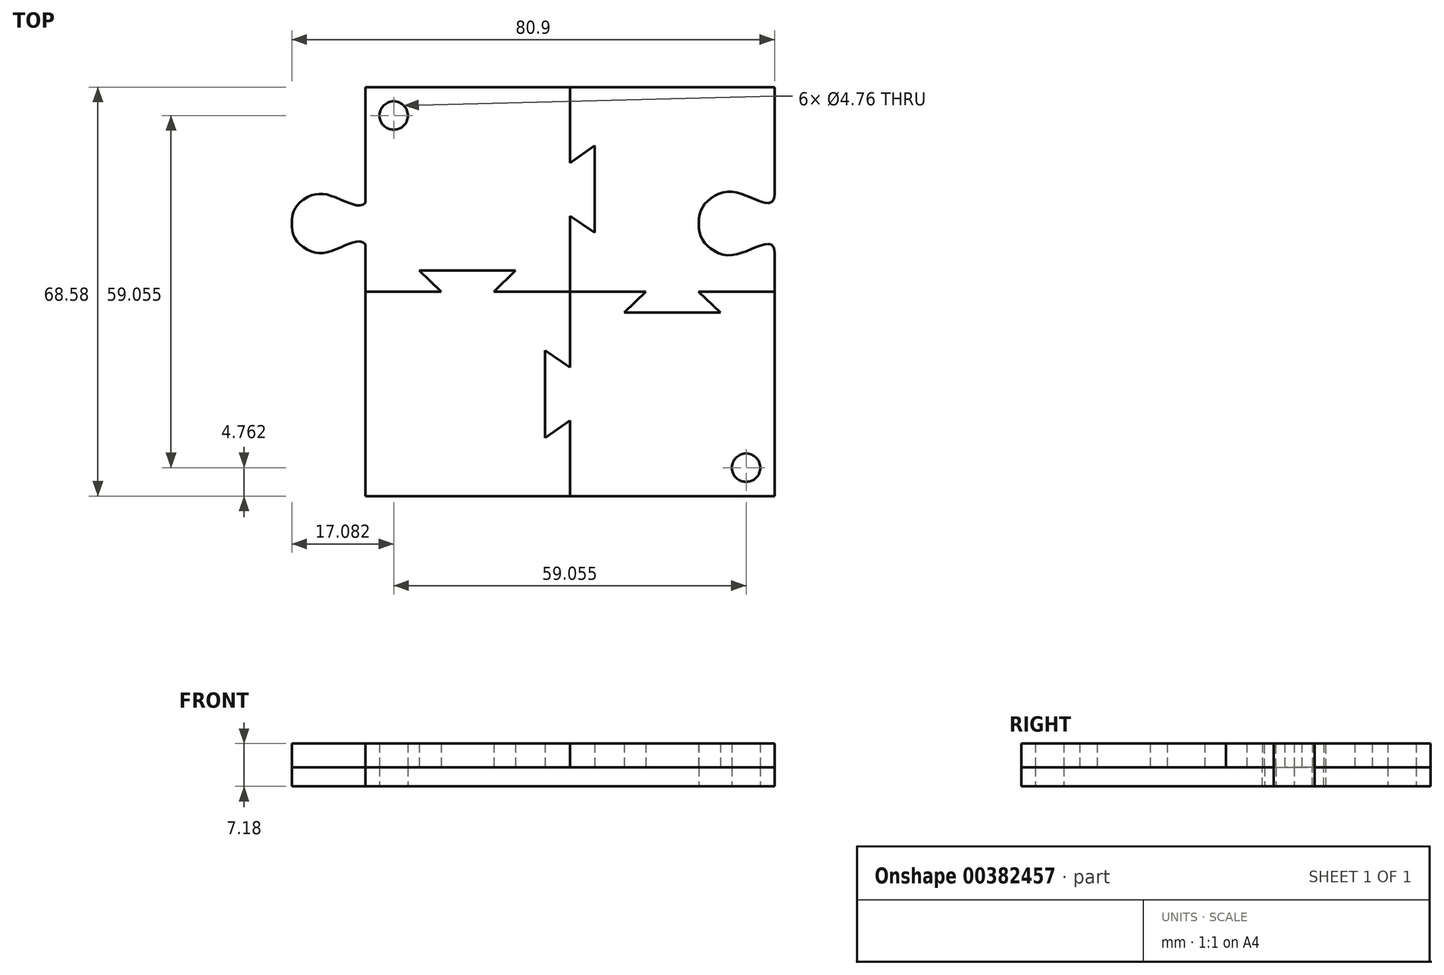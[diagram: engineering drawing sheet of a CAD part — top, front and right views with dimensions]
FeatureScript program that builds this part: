
annotation { "Feature Type Name" : "Feature", "Feature Type Description" : "" }
export const myFeature = defineFeature(function(context is Context, id is Id, definition is map)
    precondition{}
    {
        {
            var Q0;
            Q0=qCreatedBy(makeId("Top.planeOp"),FACE);
            var sketch = newSketch(context, id + "F0", { "sketchPlane" : qUnion([Q0])});
            skLineSegment(sketch, "E0.bottom", {"start": v(34.3, 34.3) * mm, "end": v(-34.3, 34.3) * mm});
            skLineSegment(sketch, "E0.top", {"start": v(34.3, -34.3) * mm, "end": v(-34.3, -34.3) * mm});
            skLineSegment(sketch, "E0.left", {"start": v(34.3, 34.3) * mm, "end": v(34.3, -34.3) * mm});
            skLineSegment(sketch, "E0.right", {"start": v(-34.3, 34.3) * mm, "end": v(-34.3, -34.3) * mm});
            skPoint(sketch, "E0.middle", {"position": v(0, 0) * mm});
            skCircle(sketch, "E1", {"center": v(-29.53, 29.53) * mm, "radius": 2.38 * mm});
            skCircle(sketch, "E2.MirrorC", {"center": v(29.53, -29.53) * mm, "radius": 2.38 * mm});
            skSolve(sketch);
        }
        {
            var Q0;
            Q0=qSketchRegion(id+"F0",true);
            extrude(context, id + "F1", {"entities" : qUnion([Q0]), "depth" : 3.17 * mm});
        }
        {
            var Q0;
            Q0=qCreatedBy(makeId("Top.planeOp"),FACE);
            var sketch = newSketch(context, id + "F2", { "sketchPlane" : qUnion([Q0])});
            skPoint(sketch, "E3", {"position": v(-34.3, 16.33) * mm});
            skPoint(sketch, "E4", {"position": v(-36.2, 14.99) * mm});
            skPoint(sketch, "E5", {"position": v(-41.66, 16.76) * mm});
            skPoint(sketch, "E6", {"position": v(-45.72, 14.99) * mm});
            skPoint(sketch, "E7", {"position": v(-47, 11.43) * mm});
            skFitSpline(sketch, "E8", {"points": [v(-34.3, 16.33) * mm, v(-36.2, 14.99) * mm, v(-41.66, 16.76) * mm, v(-45.72, 14.99) * mm, v(-47, 11.43) * mm], "startDerivative": vector(0, -24.54) * mm, "endDerivative": vector(0, -20.15) * mm});
            skLineSegment(sketch, "E9", {"start": v(-47, 11.43) * mm, "end": v(-29.95, 11.43) * mm, "construction": true});
            skFitSpline(sketch, "E10.MirrorCS", {"points": [v(-34.3, 6.53) * mm, v(-36.2, 7.87) * mm, v(-41.66, 6.1) * mm, v(-45.72, 7.87) * mm, v(-47, 11.43) * mm], "startDerivative": vector(0, 24.54) * mm, "endDerivative": vector(0, 20.15) * mm});
            skLineSegment(sketch, "E11", {"start": v(-34.3, 16.33) * mm, "end": v(-34.3, 6.53) * mm, "construction": true});
            skFitSpline(sketch, "E12.MirrorCS", {"points": [v(-34.3, 16.33) * mm, v(-32.39, 14.99) * mm, v(-26.92, 16.76) * mm, v(-22.86, 14.99) * mm, v(-21.59, 11.43) * mm], "startDerivative": vector(0, -24.54) * mm, "endDerivative": vector(0, -20.15) * mm});
            skFitSpline(sketch, "E13.MirrorCS", {"points": [v(-34.3, 6.53) * mm, v(-32.39, 7.87) * mm, v(-26.92, 6.1) * mm, v(-22.86, 7.87) * mm, v(-21.59, 11.43) * mm], "startDerivative": vector(0, 24.54) * mm, "endDerivative": vector(0, 20.15) * mm});
            skFitSpline(sketch, "E14.0", {"points": [v(-33.9, 6.53) * mm, v(-33.9, 6.8) * mm, v(-33.96, 7.3) * mm, v(-34.16, 7.77) * mm, v(-34.42, 8.07) * mm, v(-34.73, 8.28) * mm, v(-35.16, 8.4) * mm, v(-35.7, 8.38) * mm, v(-36.22, 8.27) * mm, v(-36.76, 8.1) * mm, v(-37.5, 7.83) * mm, v(-38.44, 7.42) * mm, v(-39.6, 6.94) * mm, v(-40.54, 6.64) * mm, v(-41.28, 6.5) * mm, v(-41.8, 6.46) * mm, v(-42.32, 6.5) * mm, v(-43, 6.62) * mm, v(-43.8, 6.91) * mm, v(-44.68, 7.44) * mm, v(-45.29, 7.96) * mm, v(-45.69, 8.4) * mm, v(-46.02, 8.85) * mm, v(-46.33, 9.45) * mm, v(-46.56, 10.3) * mm, v(-46.6, 11.03) * mm, v(-46.6, 11.43) * mm]});
            skFitSpline(sketch, "E14.1", {"points": [v(-33.9, 16.33) * mm, v(-33.9, 16.05) * mm, v(-33.96, 15.56) * mm, v(-34.16, 15.09) * mm, v(-34.42, 14.8) * mm, v(-34.73, 14.58) * mm, v(-35.16, 14.46) * mm, v(-35.7, 14.48) * mm, v(-36.22, 14.6) * mm, v(-36.76, 14.76) * mm, v(-37.5, 15.03) * mm, v(-38.44, 15.44) * mm, v(-39.6, 15.92) * mm, v(-40.54, 16.22) * mm, v(-41.28, 16.36) * mm, v(-41.8, 16.4) * mm, v(-42.32, 16.37) * mm, v(-43, 16.24) * mm, v(-43.8, 15.95) * mm, v(-44.68, 15.42) * mm, v(-45.29, 14.9) * mm, v(-45.69, 14.46) * mm, v(-46.02, 14.01) * mm, v(-46.33, 13.41) * mm, v(-46.56, 12.55) * mm, v(-46.6, 11.83) * mm, v(-46.6, 11.43) * mm]});
            skLineSegment(sketch, "E15", {"start": v(-34.3, 16.33) * mm, "end": v(-34.3, 6.53) * mm});
            skLineSegment(sketch, "E16", {"start": v(-34.3, 7.92) * mm, "end": v(-34.3, 14.94) * mm});
            skFitSpline(sketch, "E17.MirrorCS", {"points": [v(34.3, 16.33) * mm, v(32.39, 14.99) * mm, v(26.92, 16.76) * mm, v(22.86, 14.99) * mm, v(21.59, 11.43) * mm], "startDerivative": vector(0, -24.54) * mm, "endDerivative": vector(0, -20.15) * mm});
            skFitSpline(sketch, "E18.MirrorCS", {"points": [v(34.3, 6.53) * mm, v(32.39, 7.87) * mm, v(26.92, 6.1) * mm, v(22.86, 7.87) * mm, v(21.59, 11.43) * mm], "startDerivative": vector(0, 24.54) * mm, "endDerivative": vector(0, 20.15) * mm});
            skLineSegment(sketch, "E19", {"start": v(34.3, 16.33) * mm, "end": v(39.12, 16.33) * mm});
            skLineSegment(sketch, "E20", {"start": v(39.12, 16.33) * mm, "end": v(39.12, 6.53) * mm});
            skLineSegment(sketch, "E21", {"start": v(39.12, 6.53) * mm, "end": v(34.3, 6.53) * mm});
            skSolve(sketch);
        }
        {
            var Q0;
            Q0=makeQuery(id+"F2.imprint","IMPRINT",FACE,{"disambiguationData":[TD([[makeQuery(id+"F2.imprint","IMPRINT",EDGE,{"derivedFrom":sQuery(id+"F2.wireOp",EDGE,"E14.0")}),-1.0]])]});
            var Q1;
            Q1=makeQuery(id+"F1.opExtrude","CAP_FACE",FACE,{"disambiguationData":[OSD([sQuery(id+"F0.wireOp",EDGE,"E0.bottom"),sQuery(id+"F0.wireOp",EDGE,"E0.top"),sQuery(id+"F0.wireOp",EDGE,"E0.left"),sQuery(id+"F0.wireOp",EDGE,"E0.right"),sQuery(id+"F0.wireOp",EDGE,"E1"),sQuery(id+"F0.wireOp",EDGE,"e1648c08-8adf-473f-9b64-c467cf328ef90.MirrorC"),sQuery(id+"F0.wireOp",EDGE,"1cdcda55-2210-49d8-b5f0-9198a802923b0.MirrorC"),sQuery(id+"F0.wireOp",EDGE,"E2.MirrorC")])],"isStart":false});
            extrude(context, id + "F3", {"entities" : qUnion([Q0]), "operationType" : NewBodyOperationType.ADD, "endBound" : BoundingType.UP_TO_SURFACE, "endBoundEntityFace" : qUnion([Q1]), "depth" : 25.4 * mm});
        }
        {
            var Q0;
            Q0=qCreatedBy(makeId("Right.planeOp"),FACE);
            var sketch = newSketch(context, id + "F4", { "sketchPlane" : qUnion([Q0])});
            skLineSegment(sketch, "E22", {"start": v(0, -65.87) * mm, "end": v(0, 47.63) * mm});
            skSolve(sketch);
        }
        {
            var Q0;
            Q0=makeQuery(id+"F2.imprint","IMPRINT",FACE,{"disambiguationData":[TD([[makeQuery(id+"F2.imprint","IMPRINT",EDGE,{"derivedFrom":sQuery(id+"F2.wireOp",EDGE,"E17.MirrorCS")}),1.0]])]});
            extrude(context, id + "F5", {"entities" : qUnion([Q0]), "operationType" : NewBodyOperationType.REMOVE, "endBound" : BoundingType.THROUGH_ALL, "depth" : 25.4 * mm});
        }
        {
            var Q0;
            {var subQ0=sQuery(id+"F0.wireOp",EDGE,"E2.MirrorC");var subQ1=sQuery(id+"F0.wireOp",EDGE,"E1");var subQ2=sQuery(id+"F0.wireOp",EDGE,"E0.right");var subQ3=sQuery(id+"F0.wireOp",EDGE,"E0.left");var subQ4=sQuery(id+"F0.wireOp",EDGE,"E0.top");var subQ5=sQuery(id+"F0.wireOp",EDGE,"E0.bottom");Q0=makeQuery(id+"FDfX84p6046V9zH_1.3.F3.boolean.opBoolean","MERGE",FACE,{"derivedFrom":[makeQuery(id+"FDfX84p6046V9zH_1.2.F3.boolean.opBoolean","MERGE",FACE,{"derivedFrom":[makeQuery(id+"FDfX84p6046V9zH_1.1.F3.boolean.opBoolean","MERGE",FACE,{"derivedFrom":[makeQuery(id+"F3.boolean.opBoolean","MERGE",FACE,{"derivedFrom":[makeQuery(id+"F1.opExtrude","CAP_FACE",FACE,{"disambiguationData":[OSD([subQ5,subQ4,subQ3,subQ2,subQ1,subQ0])],"isStart":false}),makeQuery(id+"F3.opExtrude","CAP_FACE",FACE,{"disambiguationData":[OSD([subQ5,subQ4,subQ3,subQ2,subQ1,subQ0])],"isStart":false})]}),makeQuery(id+"FDfX84p6046V9zH_1.1.F3.opExtrude","CAP_FACE",FACE,{"disambiguationData":[OSD([subQ5,subQ4,subQ3,subQ2,subQ1,subQ0])],"isStart":false})]}),makeQuery(id+"FDfX84p6046V9zH_1.2.F3.opExtrude","CAP_FACE",FACE,{"disambiguationData":[OSD([subQ5,subQ4,subQ3,subQ2,subQ1,subQ0])],"isStart":false})]}),makeQuery(id+"FDfX84p6046V9zH_1.3.F3.opExtrude","CAP_FACE",FACE,{"disambiguationData":[OSD([subQ5,subQ4,subQ3,subQ2,subQ1,subQ0])],"isStart":false})]});}
            var sketch = newSketch(context, id + "F6", { "sketchPlane" : qUnion([Q0])});
            skLineSegment(sketch, "E23", {"start": v(-34.3, 0) * mm, "end": v(-21.58, 0) * mm});
            skLineSegment(sketch, "E24", {"start": v(-21.58, 0) * mm, "end": v(-25.25, 3.52) * mm});
            skLineSegment(sketch, "E25", {"start": v(0, 0) * mm, "end": v(-12.73, 0) * mm});
            skLineSegment(sketch, "E26", {"start": v(-12.73, 0) * mm, "end": v(-9.11, 3.52) * mm});
            skLineSegment(sketch, "E27", {"start": v(-9.11, 3.52) * mm, "end": v(-25.25, 3.52) * mm});
            skLineSegment(sketch, "E28.MirrorCS", {"start": v(34.3, 0) * mm, "end": v(21.58, 0) * mm});
            skLineSegment(sketch, "E29.MirrorCS", {"start": v(0, 0) * mm, "end": v(12.73, 0) * mm});
            skLineSegment(sketch, "E30.MirrorCS", {"start": v(9.11, -3.52) * mm, "end": v(25.25, -3.52) * mm});
            skLineSegment(sketch, "E31.MirrorCS", {"start": v(12.73, 0) * mm, "end": v(9.11, -3.52) * mm});
            skLineSegment(sketch, "E32.MirrorCS", {"start": v(21.58, 0) * mm, "end": v(25.25, -3.52) * mm});
            skPoint(sketch, "E33.MirrorCS.start.orphan", {"position": v(-12.73, 0) * mm});
            skPoint(sketch, "E34.MirrorCS.start.orphan", {"position": v(-21.58, 0) * mm});
            skLineSegment(sketch, "E35", {"start": v(0, 34.3) * mm, "end": v(0, 21.6) * mm});
            skLineSegment(sketch, "E36", {"start": v(0, 21.6) * mm, "end": v(4.16, 24.51) * mm});
            skLineSegment(sketch, "E37", {"start": v(0, 0) * mm, "end": v(0, 12.7) * mm});
            skLineSegment(sketch, "E38", {"start": v(0, 12.7) * mm, "end": v(4.16, 9.86) * mm});
            skLineSegment(sketch, "E39", {"start": v(4.16, 9.86) * mm, "end": v(4.16, 24.51) * mm});
            skLineSegment(sketch, "E40.MirrorCS", {"start": v(0, 0) * mm, "end": v(0, -12.7) * mm});
            skLineSegment(sketch, "E41.MirrorCS", {"start": v(0, -34.3) * mm, "end": v(0, -21.6) * mm});
            skLineSegment(sketch, "E42.MirrorCS", {"start": v(0, -12.7) * mm, "end": v(-4.16, -9.86) * mm});
            skLineSegment(sketch, "E43.MirrorCS", {"start": v(-4.16, -9.86) * mm, "end": v(-4.16, -24.51) * mm});
            skLineSegment(sketch, "E44.MirrorCS", {"start": v(0, -21.6) * mm, "end": v(-4.16, -24.51) * mm});
            skPoint(sketch, "E45.MirrorCS.start.orphan", {"position": v(0, -12.7) * mm});
            skPoint(sketch, "E46.MirrorCS.start.orphan", {"position": v(0, -21.6) * mm});
            skSolve(sketch);
        }
        {
            var Q0;
            {var subQ1=sQuery(id+"F6.wireOp",EDGE,"E28.MirrorCS");Q0=makeQuery(id+"F6.imprint","IMPRINT",FACE,{"disambiguationData":[TD([[makeQuery(id+"F6.imprint","IMPRINT",EDGE,{"derivedFrom":subQ1}),1.0]])]});}
            extrude(context, id + "F7", {"entities" : qUnion([Q0]), "depth" : 4 * mm});
        }
        {
            var Q0;
            {var subQ22=sQuery(id+"F6.wireOp",EDGE,"E23");Q0=makeQuery(id+"F6.imprint","IMPRINT",FACE,{"disambiguationData":[TD([[makeQuery(id+"F6.imprint","IMPRINT",EDGE,{"derivedFrom":subQ22}),-1.0]])]});}
            extrude(context, id + "F8", {"entities" : qUnion([Q0]), "depth" : 4 * mm});
        }
        {
            var Q0;
            {var subQ21=sQuery(id+"F6.wireOp",EDGE,"E23");Q0=makeQuery(id+"F6.imprint","IMPRINT",FACE,{"disambiguationData":[TD([[makeQuery(id+"F6.imprint","IMPRINT",EDGE,{"derivedFrom":subQ21}),1.0]])]});}
            extrude(context, id + "F9", {"entities" : qUnion([Q0]), "depth" : 4 * mm});
        }
        {
            var Q0;
            {var subQ0=sQuery(id+"F0.wireOp",EDGE,"E2.MirrorC");var subQ1=sQuery(id+"F0.wireOp",EDGE,"E1");var subQ2=sQuery(id+"F0.wireOp",EDGE,"E0.right");var subQ3=sQuery(id+"F0.wireOp",EDGE,"E0.left");var subQ4=sQuery(id+"F0.wireOp",EDGE,"E0.top");var subQ5=sQuery(id+"F0.wireOp",EDGE,"E0.bottom");Q0=makeQuery(id+"FDfX84p6046V9zH_1.3.F3.boolean.opBoolean","MERGE",FACE,{"derivedFrom":[makeQuery(id+"FDfX84p6046V9zH_1.2.F3.boolean.opBoolean","MERGE",FACE,{"derivedFrom":[makeQuery(id+"FDfX84p6046V9zH_1.1.F3.boolean.opBoolean","MERGE",FACE,{"derivedFrom":[makeQuery(id+"F3.boolean.opBoolean","MERGE",FACE,{"derivedFrom":[makeQuery(id+"F1.opExtrude","CAP_FACE",FACE,{"disambiguationData":[OSD([subQ5,subQ4,subQ3,subQ2,subQ1,subQ0])],"isStart":false}),makeQuery(id+"F3.opExtrude","CAP_FACE",FACE,{"disambiguationData":[OSD([subQ5,subQ4,subQ3,subQ2,subQ1,subQ0])],"isStart":false})]}),makeQuery(id+"FDfX84p6046V9zH_1.1.F3.opExtrude","CAP_FACE",FACE,{"disambiguationData":[OSD([subQ5,subQ4,subQ3,subQ2,subQ1,subQ0])],"isStart":false})]}),makeQuery(id+"FDfX84p6046V9zH_1.2.F3.opExtrude","CAP_FACE",FACE,{"disambiguationData":[OSD([subQ5,subQ4,subQ3,subQ2,subQ1,subQ0])],"isStart":false})]}),makeQuery(id+"FDfX84p6046V9zH_1.3.F3.opExtrude","CAP_FACE",FACE,{"disambiguationData":[OSD([subQ5,subQ4,subQ3,subQ2,subQ1,subQ0])],"isStart":false})]});}
            extrude(context, id + "F10", {"entities" : qUnion([Q0]), "depth" : 4 * mm});
        }
    });
